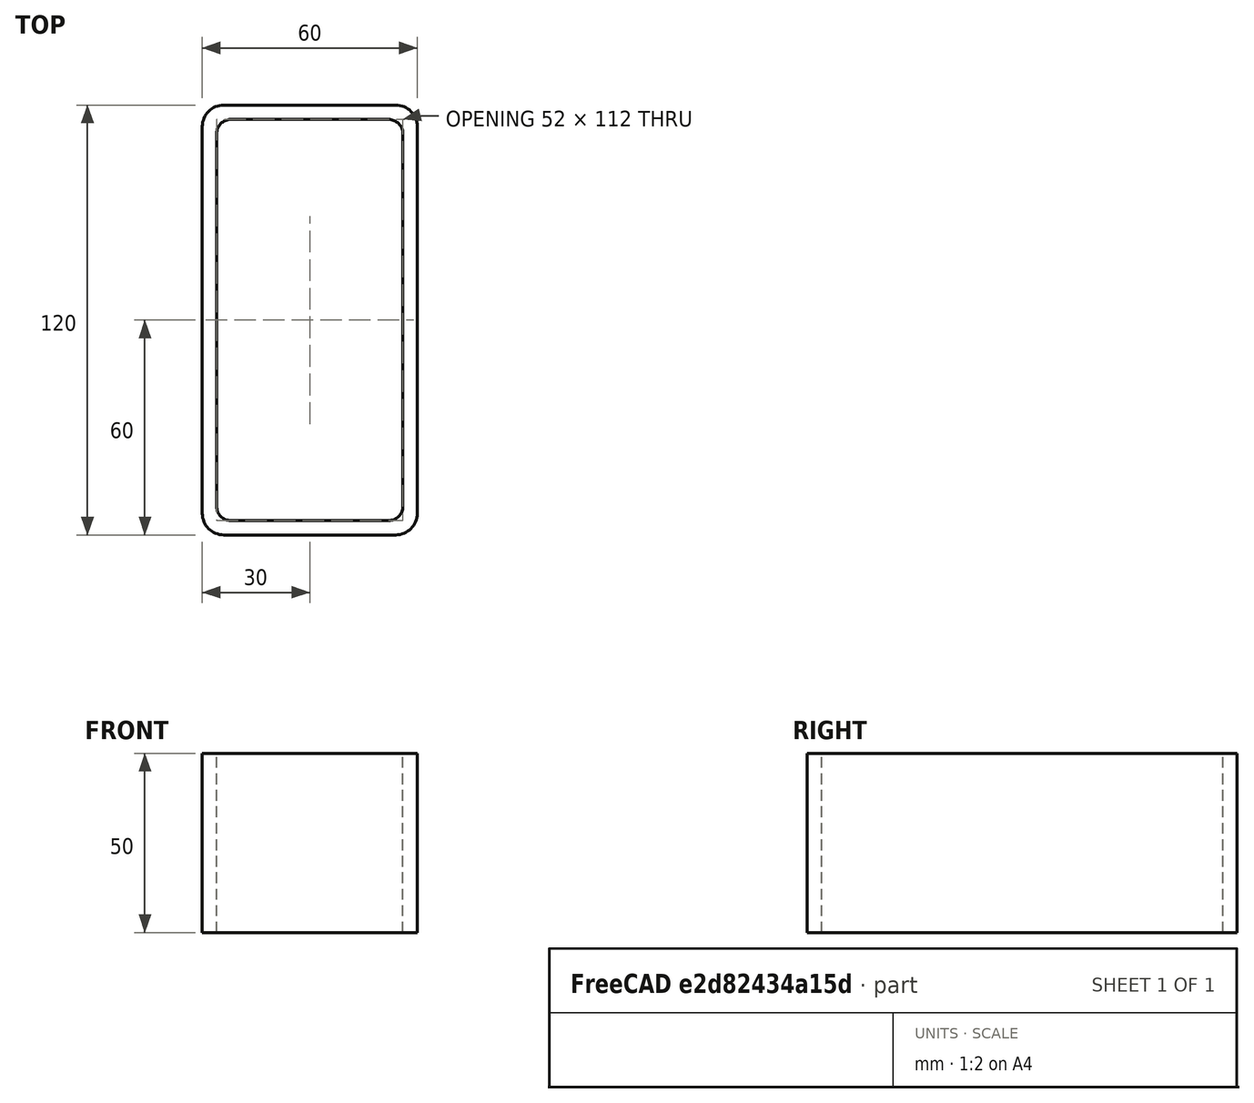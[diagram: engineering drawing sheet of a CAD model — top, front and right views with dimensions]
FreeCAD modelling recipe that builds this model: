
FCSTD DOCUMENT  (FreeCAD 0.15R4671 (Git))
Label: Rectangular hollow section 120x60x4 EN10219 S235JRH
License: All rights reserved
LicenseURL: http://en.wikipedia.org/wiki/All_rights_reserved
objects: Sketcher::SketchObject×1, Part::Extrusion×1
note: 2 computed .brp shape members not serialized (recipe doc carries the construction recipe); baked Part::Feature solids carry a one-line shape summary decoded from their .brp

FEATURE [Sketcher::SketchObject] Sketch
  sketch-geometry (16):
    g0: LineSegment StartX=-22 StartY=56 StartZ=0 EndX=22 EndY=56 EndZ=0
    g1: LineSegment StartX=26 StartY=52 StartZ=0 EndX=26 EndY=-52 EndZ=0
    g2: LineSegment StartX=22 StartY=-56 StartZ=0 EndX=-22 EndY=-56 EndZ=0
    g3: LineSegment StartX=-26 StartY=-52 StartZ=0 EndX=-26 EndY=52 EndZ=0
    g4: LineSegment StartX=-24 StartY=60 StartZ=0 EndX=24 EndY=60 EndZ=0
    g5: LineSegment StartX=30 StartY=54 StartZ=0 EndX=30 EndY=-54 EndZ=0
    g6: LineSegment StartX=24 StartY=-60 StartZ=0 EndX=-24 EndY=-60 EndZ=0
    g7: LineSegment StartX=-30 StartY=-54 StartZ=0 EndX=-30 EndY=54 EndZ=0
    g8: ArcOfCircle CenterX=-22 CenterY=52 CenterZ=0 NormalX=0 NormalY=0 NormalZ=1 Radius=4 StartAngle=1.5708 EndAngle=3.14159
    g9: ArcOfCircle CenterX=22 CenterY=52 CenterZ=0 NormalX=0 NormalY=0 NormalZ=1 Radius=4 StartAngle=0 EndAngle=1.5708
    g10: ArcOfCircle CenterX=22 CenterY=-52 CenterZ=0 NormalX=0 NormalY=0 NormalZ=1 Radius=4 StartAngle=4.71239 EndAngle=6.28319
    g11: ArcOfCircle CenterX=-22 CenterY=-52 CenterZ=0 NormalX=0 NormalY=0 NormalZ=1 Radius=4 StartAngle=3.14159 EndAngle=4.71239
    g12: ArcOfCircle CenterX=24 CenterY=54 CenterZ=0 NormalX=0 NormalY=0 NormalZ=1 Radius=6 StartAngle=0 EndAngle=1.5708
    g13: ArcOfCircle CenterX=24 CenterY=-54 CenterZ=0 NormalX=0 NormalY=0 NormalZ=1 Radius=6 StartAngle=4.71239 EndAngle=6.28319
    g14: ArcOfCircle CenterX=-24 CenterY=-54 CenterZ=0 NormalX=0 NormalY=0 NormalZ=1 Radius=6 StartAngle=3.14159 EndAngle=4.71239
    g15: ArcOfCircle CenterX=-24 CenterY=54 CenterZ=0 NormalX=0 NormalY=0 NormalZ=1 Radius=6 StartAngle=1.5708 EndAngle=3.14159
  constraints (36):
    c: Horizontal(g2)
    c: Vertical(g3)
    c: Horizontal(g6)
    c: Vertical(g7)
    c: Tangent(g3,g8) = 1.5708
    c: Tangent(g0,g8) = 1.5708
    c: Tangent(g0,g9) = 1.5708
    c: Tangent(g1,g9) = 1.5708
    c: Tangent(g1,g10) = 1.5708
    c: Tangent(g2,g10) = 1.5708
    c: Tangent(g2,g11) = 1.5708
    c: Tangent(g3,g11) = 1.5708
    c: Tangent(g4,g12) = 1.5708
    c: Tangent(g5,g12) = 1.5708
    c: Tangent(g5,g13) = 1.5708
    c: Tangent(g6,g13) = 1.5708
    c: Tangent(g6,g14) = 1.5708
    c: Tangent(g7,g14) = 1.5708
    c: Tangent(g7,g15) = 1.5708
    c: Tangent(g4,g15) = 1.5708
    c: Equal(g9,g8)
    c: Equal(g9,g11)
    c: Equal(g9,g10)
    c: Equal(g12,g15)
    c: Equal(g12,g14)
    c: Equal(g12,g13)
    c: Symmetric(g4,g6,g-1)
    c: Symmetric(g7,g5,g-2)
    c: DistanceY(g4,g6) = -120
    c: DistanceX(g7,g5) = 60
    c: Symmetric(g3,g1,g-2)
    c: Symmetric(g0,g2,g-1)
    c: DistanceY(g0,g4) = 4
    c: DistanceX(g5,g1) = -4
    c: Radius(g9) = 4
    c: Radius(g12) = 6
FEATURE [Part::Extrusion] Extrude  label="Rectangular hollow section 120x60x4 EN10219 S235JRH"
  Base = -> Sketch
  Dir = (0,0,50)
  Solid = true
